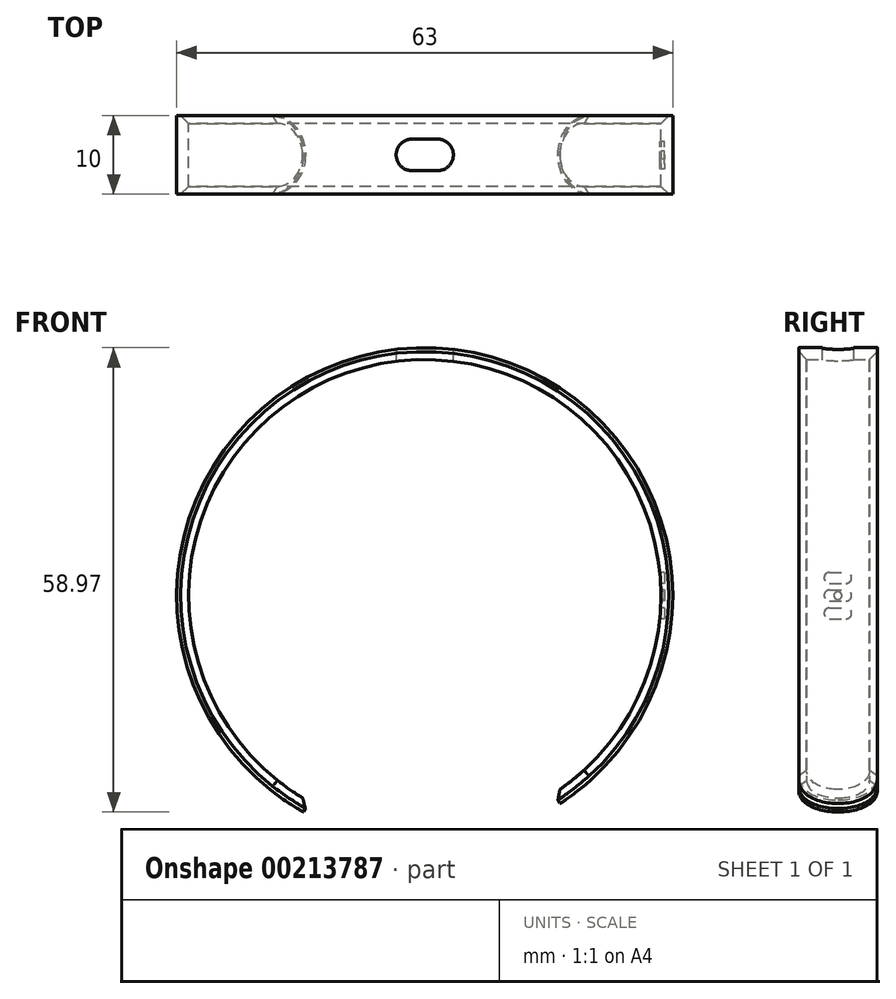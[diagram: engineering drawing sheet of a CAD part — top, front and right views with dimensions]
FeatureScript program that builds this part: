
annotation { "Feature Type Name" : "Feature", "Feature Type Description" : "" }
export const myFeature = defineFeature(function(context is Context, id is Id, definition is map)
    precondition{}
    {
        {
            var Q0;
            Q0=qCreatedBy(makeId("Front.planeOp"),FACE);
            var sketch = newSketch(context, id + "F0", { "sketchPlane" : qUnion([Q0])});
            skCircle(sketch, "E0", {"center": v(0, 0) * mm, "radius": 30 * mm});
            skCircle(sketch, "E1.0", {"center": v(0, 0) * mm, "radius": 31.5 * mm});
            skLineSegment(sketch, "E2.bottom", {"start": v(3.63, 31.29) * mm, "end": v(-3.63, 31.29) * mm, "construction": true});
            skLineSegment(sketch, "E2.top", {"start": v(3.63, 33.45) * mm, "end": v(-3.63, 33.45) * mm});
            skLineSegment(sketch, "E2.left", {"start": v(3.63, 31.29) * mm, "end": v(3.63, 33.45) * mm});
            skLineSegment(sketch, "E2.right", {"start": v(-3.63, 31.29) * mm, "end": v(-3.63, 33.45) * mm});
            skPoint(sketch, "E2.middle", {"position": v(0, 32.37) * mm});
            skLineSegment(sketch, "E3.1.0", {"start": v(-25.28, -18.8) * mm, "end": v(-27.15, -19.87) * mm});
            skLineSegment(sketch, "E3.1.1", {"start": v(-28.91, -12.5) * mm, "end": v(-30.78, -13.58) * mm});
            skLineSegment(sketch, "E3.1.2", {"start": v(-30.78, -13.58) * mm, "end": v(-27.15, -19.87) * mm});
            skLineSegment(sketch, "E3.1.3", {"start": v(-28.91, -12.5) * mm, "end": v(-25.28, -18.8) * mm, "construction": true});
            skLineSegment(sketch, "E3.2.0", {"start": v(28.91, -12.5) * mm, "end": v(30.78, -13.58) * mm});
            skLineSegment(sketch, "E3.2.1", {"start": v(25.28, -18.8) * mm, "end": v(27.15, -19.87) * mm});
            skLineSegment(sketch, "E3.2.2", {"start": v(27.15, -19.87) * mm, "end": v(30.78, -13.58) * mm});
            skLineSegment(sketch, "E3.2.3", {"start": v(25.28, -18.8) * mm, "end": v(28.91, -12.5) * mm, "construction": true});
            skLineSegment(sketch, "E4", {"start": v(0, 0) * mm, "end": v(22.27, 22.27) * mm, "construction": true});
            skLineSegment(sketch, "E5", {"start": v(0, 0) * mm, "end": v(-22.27, 22.27) * mm, "construction": true});
            skLineSegment(sketch, "E6.MirrorCS", {"start": v(0, 0) * mm, "end": v(22.27, -22.27) * mm, "construction": true});
            skLineSegment(sketch, "E7.MirrorCS", {"start": v(0, 0) * mm, "end": v(-22.27, -22.27) * mm, "construction": true});
            skLineSegment(sketch, "E8.0", {"start": v(-0.14, 0.14) * mm, "end": v(0, 0.28) * mm});
            skLineSegment(sketch, "E9.MirrorCS", {"start": v(0.14, -0.14) * mm, "end": v(0.28, 0) * mm});
            skLineSegment(sketch, "E10.MirrorCS", {"start": v(0.14, 0.14) * mm, "end": v(0, 0.28) * mm});
            skLineSegment(sketch, "E11.MirrorCS", {"start": v(-0.14, -0.14) * mm, "end": v(-0.28, 0) * mm});
            skLineSegment(sketch, "E12.MirrorCS", {"start": v(0.14, 0.14) * mm, "end": v(0.28, 0) * mm});
            skLineSegment(sketch, "E13.MirrorCS", {"start": v(-0.14, -0.14) * mm, "end": v(0, -0.28) * mm});
            skLineSegment(sketch, "E14.MirrorCS", {"start": v(0.14, -0.14) * mm, "end": v(0, -0.28) * mm});
            skLineSegment(sketch, "E15.MirrorCS", {"start": v(-0.14, 0.14) * mm, "end": v(-0.28, 0) * mm});
            skLineSegment(sketch, "E16.trimOffspring", {"start": v(-7.2, -7.48) * mm, "end": v(-21.07, -21.35) * mm, "construction": true});
            skLineSegment(sketch, "E17.trimOffspring", {"start": v(-7.48, -7.2) * mm, "end": v(-21.35, -21.07) * mm, "construction": true});
            skLineSegment(sketch, "E18.trimOffspring", {"start": v(-7.48, 7.2) * mm, "end": v(-21.35, 21.07) * mm, "construction": true});
            skLineSegment(sketch, "E19.trimOffspring", {"start": v(-7.2, 7.48) * mm, "end": v(-21.07, 21.35) * mm, "construction": true});
            skLineSegment(sketch, "E20.trimOffspring", {"start": v(7.2, 7.48) * mm, "end": v(21.07, 21.35) * mm, "construction": true});
            skLineSegment(sketch, "E21.trimOffspring", {"start": v(7.48, 7.2) * mm, "end": v(21.35, 21.07) * mm, "construction": true});
            skLineSegment(sketch, "E22.trimOffspring", {"start": v(7.2, -7.48) * mm, "end": v(21.07, -21.35) * mm, "construction": true});
            skLineSegment(sketch, "E23.trimOffspring", {"start": v(7.48, -7.2) * mm, "end": v(21.35, -21.07) * mm, "construction": true});
            skLineSegment(sketch, "E24", {"start": v(-3.63, 31.29) * mm, "end": v(-3.63, 28.18) * mm});
            skLineSegment(sketch, "E25", {"start": v(-3.63, 28.18) * mm, "end": v(3.63, 28.18) * mm});
            skLineSegment(sketch, "E26", {"start": v(3.63, 28.18) * mm, "end": v(3.63, 31.29) * mm});
            skLineSegment(sketch, "E27", {"start": v(28.91, -12.5) * mm, "end": v(7.27, 0) * mm});
            skLineSegment(sketch, "E28", {"start": v(25.28, -18.8) * mm, "end": v(3.35, -6.13) * mm});
            skLineSegment(sketch, "E29", {"start": v(3.35, -6.13) * mm, "end": v(7.27, 0) * mm});
            skLineSegment(sketch, "E30", {"start": v(-25.28, -18.8) * mm, "end": v(-3.28, -6.1) * mm});
            skLineSegment(sketch, "E31", {"start": v(-28.91, -12.5) * mm, "end": v(-6.86, 0.24) * mm});
            skLineSegment(sketch, "E32", {"start": v(-6.86, 0.24) * mm, "end": v(-3.28, -6.1) * mm});
            skLineSegment(sketch, "E33", {"start": v(0, 0.28) * mm, "end": v(1.04, -31.48) * mm, "construction": true});
            skLineSegment(sketch, "E34", {"start": v(0, -0.28) * mm, "end": v(19.14, -25.02) * mm});
            skLineSegment(sketch, "E35.MirrorCS", {"start": v(0.04, -0.28) * mm, "end": v(-17.45, -26.21) * mm});
            skLineSegment(sketch, "E36", {"start": v(0, 0) * mm, "end": v(-15.42, -27.47) * mm});
            skLineSegment(sketch, "E37.MirrorCS", {"start": v(0.02, 0) * mm, "end": v(17.2, -26.4) * mm});
            skSolve(sketch);
        }
        {
            var Q0;
            {var subQ0=sQuery(id+"F0.wireOp",EDGE,"E28");var subQ1=sQuery(id+"F0.wireOp",EDGE,"E0");var subQ2=makeQuery(id+"F0.imprint","INTERSECT",VERTEX,{"derivedFrom":[subQ1,subQ0]});Q0=makeQuery(id+"F0.imprint","IMPRINT",FACE,{"disambiguationData":[TD([[makeQuery(id+"F0.imprint","IMPRINT",EDGE,{"disambiguationData":[TD([[subQ2,-1.0]])],"derivedFrom":subQ1}),-1.0]])]});}
            var Q1;
            {var subQ0=sQuery(id+"F0.wireOp",EDGE,"E26");var subQ1=sQuery(id+"F0.wireOp",EDGE,"E0");var subQ2=makeQuery(id+"F0.imprint","INTERSECT",VERTEX,{"derivedFrom":[subQ1,subQ0]});Q1=makeQuery(id+"F0.imprint","IMPRINT",FACE,{"disambiguationData":[TD([[makeQuery(id+"F0.imprint","IMPRINT",EDGE,{"disambiguationData":[TD([[subQ2,1.0]])],"derivedFrom":subQ1}),-1.0]])]});}
            var Q2;
            {var subQ0=sQuery(id+"F0.wireOp",EDGE,"E24");var subQ1=sQuery(id+"F0.wireOp",EDGE,"E0");var subQ2=makeQuery(id+"F0.imprint","INTERSECT",VERTEX,{"derivedFrom":[subQ1,subQ0]});Q2=makeQuery(id+"F0.imprint","IMPRINT",FACE,{"disambiguationData":[TD([[makeQuery(id+"F0.imprint","IMPRINT",EDGE,{"disambiguationData":[TD([[subQ2,1.0]])],"derivedFrom":subQ1}),-1.0]])]});}
            var Q3;
            {var subQ0=sQuery(id+"F0.wireOp",EDGE,"E24");var subQ1=sQuery(id+"F0.wireOp",EDGE,"E0");var subQ2=makeQuery(id+"F0.imprint","INTERSECT",VERTEX,{"derivedFrom":[subQ1,subQ0]});Q3=makeQuery(id+"F0.imprint","IMPRINT",FACE,{"disambiguationData":[TD([[makeQuery(id+"F0.imprint","IMPRINT",EDGE,{"disambiguationData":[TD([[subQ2,-1.0]])],"derivedFrom":subQ1}),-1.0]])]});}
            var Q4;
            {var subQ0=sQuery(id+"F0.wireOp",EDGE,"E31");var subQ1=sQuery(id+"F0.wireOp",EDGE,"E0");var subQ2=makeQuery(id+"F0.imprint","INTERSECT",VERTEX,{"derivedFrom":[subQ1,subQ0]});Q4=makeQuery(id+"F0.imprint","IMPRINT",FACE,{"disambiguationData":[TD([[makeQuery(id+"F0.imprint","IMPRINT",EDGE,{"disambiguationData":[TD([[subQ2,-1.0]])],"derivedFrom":subQ1}),-1.0]])]});}
            var Q5;
            {var subQ3=sQuery(id+"F0.wireOp",EDGE,"E0");var subQ5=makeQuery(id+"F0.imprint","INTERSECT",VERTEX,{"derivedFrom":[subQ3,sQuery(id+"F0.wireOp",EDGE,"E35.MirrorCS")]});Q5=makeQuery(id+"F0.imprint","IMPRINT",FACE,{"disambiguationData":[TD([[makeQuery(id+"F0.imprint","IMPRINT",EDGE,{"disambiguationData":[TD([[subQ5,1.0]])],"derivedFrom":subQ3}),-1.0]])]});}
            var Q6;
            {var subQ0=sQuery(id+"F0.wireOp",EDGE,"E37.MirrorCS");var subQ1=sQuery(id+"F0.wireOp",EDGE,"E0");var subQ2=makeQuery(id+"F0.imprint","INTERSECT",VERTEX,{"derivedFrom":[subQ1,subQ0]});Q6=makeQuery(id+"F0.imprint","IMPRINT",FACE,{"disambiguationData":[TD([[makeQuery(id+"F0.imprint","IMPRINT",EDGE,{"disambiguationData":[TD([[subQ2,-1.0]])],"derivedFrom":subQ1}),-1.0]])]});}
            var Q7;
            {var subQ0=sQuery(id+"F0.wireOp",EDGE,"E34");var subQ1=sQuery(id+"F0.wireOp",EDGE,"E0");var subQ2=makeQuery(id+"F0.imprint","INTERSECT",VERTEX,{"derivedFrom":[subQ1,subQ0]});Q7=makeQuery(id+"F0.imprint","IMPRINT",FACE,{"disambiguationData":[TD([[makeQuery(id+"F0.imprint","IMPRINT",EDGE,{"disambiguationData":[TD([[subQ2,-1.0]])],"derivedFrom":subQ1}),-1.0]])]});}
            extrude(context, id + "F1", {"entities" : qUnion([Q0, Q1, Q2, Q3, Q4, Q5, Q6, Q7]), "depth" : 5 * mm, "hasSecondDirection" : true, "secondDirectionOppositeDirection" : true, "secondDirectionDepth" : 5 * mm});
        }
        {
            var Q0;
            Q0=qCreatedBy(makeId("Top.planeOp"),FACE);
            var sketch = newSketch(context, id + "F2", { "sketchPlane" : qUnion([Q0])});
            skCircle(sketch, "E38", {"center": v(0, 0) * mm, "radius": 0.15 * mm});
            skCircle(sketch, "E39.1.0.0", {"center": v(0, -0.6) * mm, "radius": 0.15 * mm});
            skCircle(sketch, "E39.2.0.0", {"center": v(0, -1.2) * mm, "radius": 0.15 * mm});
            skCircle(sketch, "E39.3.0.0", {"center": v(0, -1.8) * mm, "radius": 0.15 * mm});
            skCircle(sketch, "E39.4.0.0", {"center": v(0, -2.4) * mm, "radius": 0.15 * mm});
            skCircle(sketch, "E39.5.0.0", {"center": v(0, -3) * mm, "radius": 0.15 * mm});
            skCircle(sketch, "E39.6.0.0", {"center": v(0, -3.6) * mm, "radius": 0.15 * mm});
            skLineSegment(sketch, "E39.direction1", {"start": v(0, 0) * mm, "end": v(0, -0.6) * mm, "construction": true});
            skCircle(sketch, "E40.MirrorC", {"center": v(0, 0.6) * mm, "radius": 0.15 * mm});
            skCircle(sketch, "E41.MirrorC", {"center": v(0, 1.2) * mm, "radius": 0.15 * mm});
            skCircle(sketch, "E42.MirrorC", {"center": v(0, 1.8) * mm, "radius": 0.15 * mm});
            skCircle(sketch, "E43.MirrorC", {"center": v(0, 2.4) * mm, "radius": 0.15 * mm});
            skCircle(sketch, "E44.MirrorC", {"center": v(0, 3) * mm, "radius": 0.15 * mm});
            skCircle(sketch, "E45.MirrorC", {"center": v(0, 3.6) * mm, "radius": 0.15 * mm});
            skSolve(sketch);
        }
        {
            var Q0;
            Q0=makeQuery(id+"F0.imprint","IMPRINT",FACE,{"disambiguationData":[TD([[makeQuery(id+"F0.imprint","IMPRINT",EDGE,{"derivedFrom":sQuery(id+"F0.wireOp",EDGE,"E2.top")}),1.0]])]});
            var Q1;
            {var subQ0=sQuery(id+"F0.wireOp",EDGE,"E24");var subQ1=sQuery(id+"F0.wireOp",EDGE,"E0");var subQ2=makeQuery(id+"F0.imprint","INTERSECT",VERTEX,{"derivedFrom":[subQ1,subQ0]});Q1=makeQuery(id+"F0.imprint","IMPRINT",FACE,{"disambiguationData":[TD([[makeQuery(id+"F0.imprint","IMPRINT",EDGE,{"disambiguationData":[TD([[subQ2,1.0]])],"derivedFrom":subQ1}),-1.0]])]});}
            var Q2;
            {var subQ5=sQuery(id+"F0.wireOp",EDGE,"E25");Q2=makeQuery(id+"F0.imprint","IMPRINT",FACE,{"disambiguationData":[TD([[makeQuery(id+"F0.imprint","IMPRINT",EDGE,{"derivedFrom":subQ5}),1.0]])]});}
            extrude(context, id + "F3", {"entities" : qUnion([Q0, Q1, Q2]), "operationType" : NewBodyOperationType.REMOVE, "oppositeDirection" : true, "depth" : 2 * mm, "hasSecondDirection" : true, "secondDirectionOppositeDirection" : false, "secondDirectionDepth" : 2 * mm});
        }
        {
            var Q0;
            Q0=makeQuery(id+"F1.opExtrude","CAP_EDGE",EDGE,{"disambiguationData":[OSD([sQuery(id+"F0.wireOp",EDGE,"E34")])],"isStart":false});
            var Q1;
            Q1=makeQuery(id+"F1.opExtrude","CAP_EDGE",EDGE,{"disambiguationData":[OSD([sQuery(id+"F0.wireOp",EDGE,"E34")])],"isStart":true});
            var Q2;
            Q2=makeQuery(id+"F1.opExtrude","CAP_EDGE",EDGE,{"disambiguationData":[OSD([sQuery(id+"F0.wireOp",EDGE,"E30")])],"isStart":true});
            var Q3;
            Q3=makeQuery(id+"F1.opExtrude","CAP_EDGE",EDGE,{"disambiguationData":[OSD([sQuery(id+"F0.wireOp",EDGE,"E30")])],"isStart":false});
            var Q4;
            Q4=makeQuery(id+"F1.opExtrude","CAP_EDGE",EDGE,{"disambiguationData":[OSD([sQuery(id+"F0.wireOp",EDGE,"E28")])],"isStart":false});
            var Q5;
            Q5=makeQuery(id+"F1.opExtrude","CAP_EDGE",EDGE,{"disambiguationData":[OSD([sQuery(id+"F0.wireOp",EDGE,"E28")])],"isStart":true});
            var Q6;
            Q6=makeQuery(id+"F1.opExtrude","CAP_EDGE",EDGE,{"disambiguationData":[OSD([sQuery(id+"F0.wireOp",EDGE,"E36")])],"isStart":true});
            var Q7;
            Q7=makeQuery(id+"F1.opExtrude","CAP_EDGE",EDGE,{"disambiguationData":[OSD([sQuery(id+"F0.wireOp",EDGE,"E36")])],"isStart":false});
            var Q8;
            Q8=makeQuery(id+"F1.opExtrude","CAP_EDGE",EDGE,{"disambiguationData":[OSD([sQuery(id+"F0.wireOp",EDGE,"E37.MirrorCS")])],"isStart":false});
            var Q9;
            Q9=makeQuery(id+"F1.opExtrude","CAP_EDGE",EDGE,{"disambiguationData":[OSD([sQuery(id+"F0.wireOp",EDGE,"E37.MirrorCS")])],"isStart":true});
            fillet(context, id + "F4", {"entities" : qUnion([Q0, Q1, Q2, Q3, Q4, Q5, Q6, Q7, Q8, Q9]), "radius" : 5 * mm, "tangentPropagation" : true, "allowEdgeOverflow" : false});
        }
        {
            var Q0;
            Q0=makeQuery(id+"F1.opExtrude","CAP_EDGE",EDGE,{"disambiguationData":[OSD([sQuery(id+"F0.wireOp",EDGE,"E0")])],"isStart":true});
            var Q1;
            Q1=makeQuery(id+"F1.opExtrude","CAP_EDGE",EDGE,{"disambiguationData":[OSD([sQuery(id+"F0.wireOp",EDGE,"E0")])],"isStart":false});
            chamfer(context, id + "F5", {"entities" : qUnion([Q0, Q1]), "width" : 1 * mm, "tangentPropagation" : true});
        }
        {
            var Q0;
            Q0=makeQuery(id+"F3.boolean.opBoolean","COPY",EDGE,{"derivedFrom":makeQuery(id+"F3.opExtrude","CAP_EDGE",EDGE,{"disambiguationData":[OSD([sQuery(id+"F0.wireOp",EDGE,"E2.left"),sQuery(id+"F0.wireOp",EDGE,"E26")])],"isStart":false})});
            var Q1;
            Q1=makeQuery(id+"F3.boolean.opBoolean","COPY",EDGE,{"derivedFrom":makeQuery(id+"F3.opExtrude","CAP_EDGE",EDGE,{"disambiguationData":[OSD([sQuery(id+"F0.wireOp",EDGE,"E2.right"),sQuery(id+"F0.wireOp",EDGE,"E24")])],"isStart":false})});
            var Q2;
            Q2=makeQuery(id+"F3.boolean.opBoolean","COPY",EDGE,{"derivedFrom":makeQuery(id+"F3.opExtrude","CAP_EDGE",EDGE,{"disambiguationData":[OSD([sQuery(id+"F0.wireOp",EDGE,"E2.right"),sQuery(id+"F0.wireOp",EDGE,"E24")])],"isStart":true})});
            var Q3;
            Q3=makeQuery(id+"F3.boolean.opBoolean","COPY",EDGE,{"derivedFrom":makeQuery(id+"F3.opExtrude","CAP_EDGE",EDGE,{"disambiguationData":[OSD([sQuery(id+"F0.wireOp",EDGE,"E2.left"),sQuery(id+"F0.wireOp",EDGE,"E26")])],"isStart":true})});
            fillet(context, id + "F6", {"entities" : qUnion([Q0, Q1, Q2, Q3]), "radius" : 2 * mm, "tangentPropagation" : true, "allowEdgeOverflow" : false});
        }
        {
            var Q0;
            Q0=qCreatedBy(makeId("Right.planeOp"),FACE);
            var sketch = newSketch(context, id + "F7", { "sketchPlane" : qUnion([Q0])});
            skLineSegment(sketch, "E46.bottom", {"start": v(-1.07, -0.68) * mm, "end": v(1.02, -0.68) * mm});
            skArc(sketch, "E47.filletArc", {"start": v(-1.07, 0.72) * mm, "mid": v(-1.57, 0.51) * mm, "end": v(-1.77, 0.02) * mm});
            skArc(sketch, "E48.filletArc", {"start": v(-1.77, 0.02) * mm, "mid": v(-1.57, -0.48) * mm, "end": v(-1.07, -0.68) * mm});
            skArc(sketch, "E49.filletArc", {"start": v(1.72, 0.02) * mm, "mid": v(1.52, 0.51) * mm, "end": v(1.02, 0.72) * mm});
            skArc(sketch, "E50.filletArc", {"start": v(1.02, -0.68) * mm, "mid": v(1.52, -0.48) * mm, "end": v(1.72, 0.02) * mm});
            skLineSegment(sketch, "E51.bottom", {"start": v(-1.07, -2.93) * mm, "end": v(1.02, -2.93) * mm});
            skLineSegment(sketch, "E51.top", {"start": v(-1.07, -1.53) * mm, "end": v(1.02, -1.53) * mm});
            skArc(sketch, "E52.filletArc", {"start": v(-1.07, -1.53) * mm, "mid": v(-1.57, -1.74) * mm, "end": v(-1.77, -2.23) * mm});
            skArc(sketch, "E53.filletArc", {"start": v(-1.77, -2.23) * mm, "mid": v(-1.57, -2.73) * mm, "end": v(-1.07, -2.93) * mm});
            skArc(sketch, "E54.filletArc", {"start": v(1.72, -2.23) * mm, "mid": v(1.52, -1.74) * mm, "end": v(1.02, -1.53) * mm});
            skArc(sketch, "E55.filletArc", {"start": v(1.02, -2.93) * mm, "mid": v(1.52, -2.73) * mm, "end": v(1.72, -2.23) * mm});
            skLineSegment(sketch, "E56", {"start": v(-1.07, 0.72) * mm, "end": v(1.02, 0.72) * mm});
            skCircle(sketch, "E57", {"center": v(-0.02, 0.02) * mm, "radius": 0.5 * mm});
            skLineSegment(sketch, "E58.bottom", {"start": v(-1.07, 1.57) * mm, "end": v(1.02, 1.57) * mm});
            skLineSegment(sketch, "E58.top", {"start": v(-1.07, 2.97) * mm, "end": v(1.02, 2.97) * mm});
            skArc(sketch, "E59.filletArc", {"start": v(-1.07, 2.97) * mm, "mid": v(-1.57, 2.77) * mm, "end": v(-1.77, 2.27) * mm});
            skArc(sketch, "E60.filletArc", {"start": v(-1.77, 2.27) * mm, "mid": v(-1.57, 1.78) * mm, "end": v(-1.07, 1.57) * mm});
            skArc(sketch, "E61.filletArc", {"start": v(1.72, 2.27) * mm, "mid": v(1.52, 2.77) * mm, "end": v(1.02, 2.97) * mm});
            skArc(sketch, "E62.filletArc", {"start": v(1.02, 1.57) * mm, "mid": v(1.52, 1.78) * mm, "end": v(1.72, 2.27) * mm});
            skSolve(sketch);
        }
        {
            var Q0;
            Q0=makeQuery(id+"F7.imprint","IMPRINT",FACE,{"disambiguationData":[TD([[makeQuery(id+"F7.imprint","IMPRINT",EDGE,{"derivedFrom":sQuery(id+"F7.wireOp",EDGE,"E58.bottom")}),1.0]])]});
            var Q1;
            Q1=makeQuery(id+"F7.imprint","IMPRINT",FACE,{"disambiguationData":[TD([[makeQuery(id+"F7.imprint","IMPRINT",EDGE,{"derivedFrom":sQuery(id+"F7.wireOp",EDGE,"E46.bottom")}),1.0]])]});
            var Q2;
            Q2=makeQuery(id+"F7.imprint","IMPRINT",FACE,{"disambiguationData":[TD([[makeQuery(id+"F7.imprint","IMPRINT",EDGE,{"derivedFrom":sQuery(id+"F7.wireOp",EDGE,"E51.bottom")}),1.0]])]});
            extrude(context, id + "F8", {"entities" : qUnion([Q0, Q1, Q2]), "operationType" : NewBodyOperationType.REMOVE, "depth" : 30.43 * mm, "offsetDistance" : 25 * mm});
        }
    });
